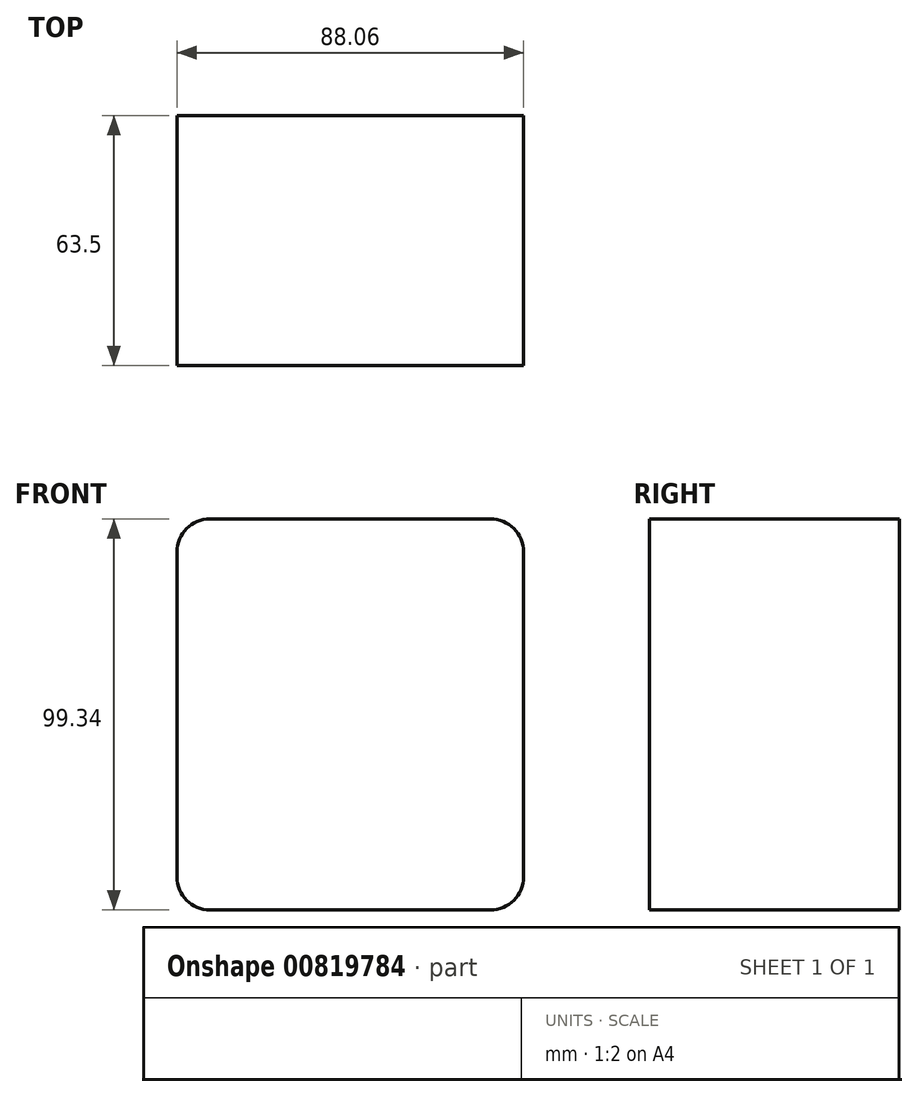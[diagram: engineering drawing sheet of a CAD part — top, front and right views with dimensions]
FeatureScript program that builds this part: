
annotation { "Feature Type Name" : "Feature", "Feature Type Description" : "" }
export const myFeature = defineFeature(function(context is Context, id is Id, definition is map)
    precondition{}
    {
        {
            var Q0;
            Q0=qCreatedBy(makeId("Front.planeOp"),FACE);
            var sketch = newSketch(context, id + "F0", { "sketchPlane" : qUnion([Q0])});
            skLineSegment(sketch, "E0.bottom", {"start": v(35.64, 49.67) * mm, "end": v(-35.64, 49.67) * mm});
            skLineSegment(sketch, "E0.top", {"start": v(35.64, -49.67) * mm, "end": v(-35.64, -49.67) * mm});
            skLineSegment(sketch, "E0.left", {"start": v(44.03, 41.29) * mm, "end": v(44.03, -41.29) * mm});
            skLineSegment(sketch, "E0.right", {"start": v(-44.03, 41.29) * mm, "end": v(-44.03, -41.29) * mm});
            skPoint(sketch, "E0.middle", {"position": v(0, 0) * mm});
            skPoint(sketch, "E1.visualSharp", {"position": v(44.03, 49.67) * mm});
            skArc(sketch, "E1.filletArc", {"start": v(44.03, 41.29) * mm, "mid": v(41.57, 47.21) * mm, "end": v(35.64, 49.67) * mm});
            skPoint(sketch, "E2.visualSharp", {"position": v(-44.03, 49.67) * mm});
            skArc(sketch, "E2.filletArc", {"start": v(-35.64, 49.67) * mm, "mid": v(-41.57, 47.21) * mm, "end": v(-44.03, 41.29) * mm});
            skPoint(sketch, "E3.visualSharp", {"position": v(-44.03, -49.67) * mm});
            skArc(sketch, "E3.filletArc", {"start": v(-44.03, -41.29) * mm, "mid": v(-41.57, -47.21) * mm, "end": v(-35.64, -49.67) * mm});
            skPoint(sketch, "E4.visualSharp", {"position": v(44.03, -49.67) * mm});
            skArc(sketch, "E4.filletArc", {"start": v(35.64, -49.67) * mm, "mid": v(41.57, -47.21) * mm, "end": v(44.03, -41.29) * mm});
            skSolve(sketch);
        }
        {
            var Q0;
            Q0=makeQuery(id+"F0.imprint","IMPRINT",FACE,{"disambiguationData":[TD([[makeQuery(id+"F0.imprint","IMPRINT",EDGE,{"derivedFrom":sQuery(id+"F0.wireOp",EDGE,"E0.bottom")}),1.0]])]});
            extrude(context, id + "F1", {"entities" : qUnion([Q0]), "depth" : 63.5 * mm, "offsetDistance" : 25.4 * mm});
        }
    });
